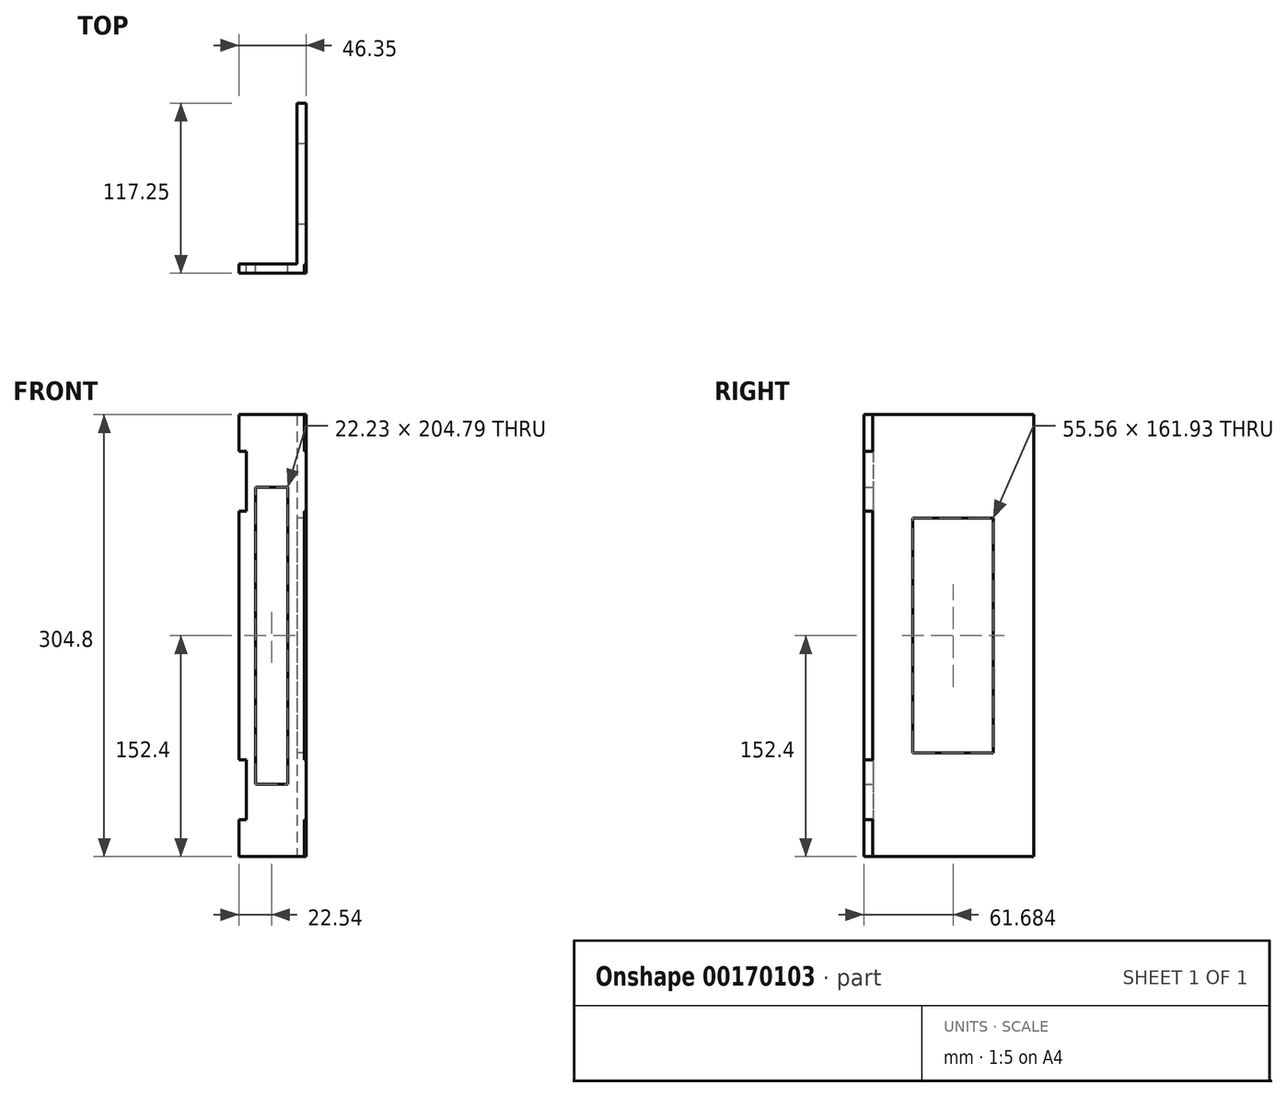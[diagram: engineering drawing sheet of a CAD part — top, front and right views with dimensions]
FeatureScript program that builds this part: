
annotation { "Feature Type Name" : "Feature", "Feature Type Description" : "" }
export const myFeature = defineFeature(function(context is Context, id is Id, definition is map)
    precondition{}
    {
        {
            var Q0;
            Q0=qCreatedBy(makeId("Front.planeOp"),FACE);
            var sketch = newSketch(context, id + "F0", { "sketchPlane" : qUnion([Q0])});
            skLineSegment(sketch, "E0.bottom", {"start": v(-7.94, 85.73) * mm, "end": v(7.94, 85.73) * mm});
            skLineSegment(sketch, "E0.top", {"start": v(-7.94, -85.73) * mm, "end": v(7.94, -85.73) * mm});
            skLineSegment(sketch, "E0.left", {"start": v(-7.94, 85.73) * mm, "end": v(-7.94, -85.73) * mm});
            skLineSegment(sketch, "E0.right", {"start": v(7.94, 85.73) * mm, "end": v(7.94, -85.73) * mm});
            skPoint(sketch, "E0.middle", {"position": v(0, 0) * mm});
            skLineSegment(sketch, "E1.bottom", {"start": v(-11.11, 102.4) * mm, "end": v(11.11, 102.4) * mm});
            skLineSegment(sketch, "E1.top", {"start": v(-11.11, -102.4) * mm, "end": v(11.11, -102.4) * mm});
            skLineSegment(sketch, "E1.left", {"start": v(-11.11, 102.4) * mm, "end": v(-11.11, -102.4) * mm});
            skLineSegment(sketch, "E1.right", {"start": v(11.11, 102.4) * mm, "end": v(11.11, -102.4) * mm});
            skCircle(sketch, "E2", {"center": v(0, 90.49) * mm, "radius": 1.2 * mm});
            skCircle(sketch, "E3.MirrorC", {"center": v(0, -90.49) * mm, "radius": 1.2 * mm});
            skLineSegment(sketch, "E4.bottom", {"start": v(-17.46, 152.4) * mm, "end": v(17.46, 152.4) * mm});
            skLineSegment(sketch, "E4.top", {"start": v(-17.46, -152.4) * mm, "end": v(17.46, -152.4) * mm});
            skLineSegment(sketch, "E4.left", {"start": v(-17.46, 127) * mm, "end": v(-17.46, 85.73) * mm});
            skLineSegment(sketch, "E4.right", {"start": v(17.46, 127) * mm, "end": v(17.46, 85.73) * mm});
            skLineSegment(sketch, "E5.bottom", {"start": v(-17.46, 152.4) * mm, "end": v(-22.54, 152.4) * mm});
            skLineSegment(sketch, "E5.right", {"start": v(-22.54, 152.4) * mm, "end": v(-22.54, 127) * mm});
            skLineSegment(sketch, "E6.bottom", {"start": v(-22.54, 127) * mm, "end": v(-17.46, 127) * mm});
            skLineSegment(sketch, "E6.top", {"start": v(-22.54, 85.73) * mm, "end": v(-17.46, 85.73) * mm});
            skLineSegment(sketch, "E7.trimOffspring", {"start": v(-22.54, 85.73) * mm, "end": v(-22.54, 0) * mm});
            skLineSegment(sketch, "E8.MirrorCS", {"start": v(-22.54, -85.73) * mm, "end": v(-22.54, 0) * mm});
            skLineSegment(sketch, "E9.MirrorCS", {"start": v(-22.54, -85.73) * mm, "end": v(-17.46, -85.73) * mm});
            skLineSegment(sketch, "E10.MirrorCS", {"start": v(-17.46, -152.4) * mm, "end": v(-22.54, -152.4) * mm});
            skLineSegment(sketch, "E11.MirrorCS", {"start": v(-22.54, -152.4) * mm, "end": v(-22.54, -127) * mm});
            skLineSegment(sketch, "E12.MirrorCS", {"start": v(-22.54, -127) * mm, "end": v(-17.46, -127) * mm});
            skLineSegment(sketch, "E13.MirrorCS", {"start": v(17.46, -152.4) * mm, "end": v(22.54, -152.4) * mm});
            skLineSegment(sketch, "E14.MirrorCS", {"start": v(22.54, -152.4) * mm, "end": v(22.54, -127) * mm});
            skLineSegment(sketch, "E15.MirrorCS", {"start": v(22.54, -127) * mm, "end": v(17.46, -127) * mm});
            skLineSegment(sketch, "E16.MirrorCS", {"start": v(22.54, -85.73) * mm, "end": v(17.46, -85.73) * mm});
            skLineSegment(sketch, "E17.MirrorCS", {"start": v(22.54, -85.73) * mm, "end": v(22.54, 0) * mm});
            skLineSegment(sketch, "E18.MirrorCS", {"start": v(22.54, 85.73) * mm, "end": v(22.54, 0) * mm});
            skLineSegment(sketch, "E19.MirrorCS", {"start": v(22.54, 85.73) * mm, "end": v(17.46, 85.73) * mm});
            skLineSegment(sketch, "E20.MirrorCS", {"start": v(22.54, 127) * mm, "end": v(17.46, 127) * mm});
            skLineSegment(sketch, "E21.MirrorCS", {"start": v(17.46, 152.4) * mm, "end": v(22.54, 152.4) * mm});
            skLineSegment(sketch, "E22.MirrorCS", {"start": v(22.54, 152.4) * mm, "end": v(22.54, 127) * mm});
            skLineSegment(sketch, "E23.trimOffspring", {"start": v(-17.46, -85.73) * mm, "end": v(-17.46, -127) * mm});
            skLineSegment(sketch, "E24.trimOffspring", {"start": v(17.46, -85.72) * mm, "end": v(17.46, -127) * mm});
            skSolve(sketch);
        }
        {
            var Q0;
            Q0=makeQuery(id+"F0.imprint","IMPRINT",FACE,{"disambiguationData":[TD([[makeQuery(id+"F0.imprint","IMPRINT",EDGE,{"derivedFrom":sQuery(id+"F0.wireOp",EDGE,"E1.bottom")}),1.0]])]});
            extrude(context, id + "F1", {"entities" : qUnion([Q0]), "depth" : 6.35 * mm});
        }
        {
            var Q0;
            Q0=qCreatedBy(makeId("Right.planeOp"),FACE);
            cPlane(context, id + "F2", {"entities" : qUnion([Q0]), "cplaneType" : CPlaneType.OFFSET, "offset" : 17.46 * mm, "width" : 152.4 * mm, "height" : 152.4 * mm});
        }
        {
            var Q0;
            Q0=qCreatedBy(id+"F2.planeOp",FACE);
            var sketch = newSketch(context, id + "F3", { "sketchPlane" : qUnion([Q0])});
            skLineSegment(sketch, "E25", {"start": v(55.33, 146.13) * mm, "end": v(55.33, -156.26) * mm, "construction": true});
            skLineSegment(sketch, "E26.bottom", {"start": v(27.55, 80.96) * mm, "end": v(83.12, 80.96) * mm});
            skLineSegment(sketch, "E26.top", {"start": v(27.55, -80.96) * mm, "end": v(83.12, -80.96) * mm});
            skLineSegment(sketch, "E26.left", {"start": v(27.55, 80.96) * mm, "end": v(27.55, -80.96) * mm});
            skLineSegment(sketch, "E26.right", {"start": v(83.12, 80.96) * mm, "end": v(83.12, -80.96) * mm});
            skPoint(sketch, "E26.middle", {"position": v(55.33, 0) * mm});
            skCircle(sketch, "E27", {"center": v(55.33, 20.64) * mm, "radius": 19.05 * mm});
            skLineSegment(sketch, "E28.bottom", {"start": v(110.9, 152.4) * mm, "end": v(-0.23, 152.4) * mm});
            skLineSegment(sketch, "E28.top", {"start": v(110.9, -152.4) * mm, "end": v(-0.23, -152.4) * mm});
            skLineSegment(sketch, "E28.left", {"start": v(110.9, 152.4) * mm, "end": v(110.9, -152.4) * mm});
            skLineSegment(sketch, "E28.right", {"start": v(-0.23, 152.4) * mm, "end": v(-0.23, 127) * mm});
            skLineSegment(sketch, "E29.0", {"start": v(-6.35, 127) * mm, "end": v(0, 127) * mm});
            skLineSegment(sketch, "E30.0", {"start": v(-6.35, 85.73) * mm, "end": v(0, 85.73) * mm});
            skLineSegment(sketch, "E31.0", {"start": v(-6.35, -85.73) * mm, "end": v(0, -85.73) * mm});
            skLineSegment(sketch, "E32.0", {"start": v(-6.35, -127) * mm, "end": v(0, -127) * mm});
            skPoint(sketch, "E33.0", {"position": v(-3.18, -152.4) * mm});
            skLineSegment(sketch, "E34.0", {"start": v(-6.35, 127) * mm, "end": v(-6.35, 85.73) * mm});
            skLineSegment(sketch, "E35.trimOffspring", {"start": v(-0.23, 85.72) * mm, "end": v(-0.23, -85.73) * mm});
            skLineSegment(sketch, "E36.0", {"start": v(-6.35, -85.72) * mm, "end": v(-6.35, -127) * mm});
            skLineSegment(sketch, "E37.trimOffspring", {"start": v(-0.23, -127) * mm, "end": v(-0.23, -152.4) * mm});
            skSolve(sketch);
        }
        {
            var Q0;
            Q0 = qSketchRegion(id + "F3", true);
            extrude(context, id + "F4", {"entities" : qUnion([Q0]), "operationType" : NewBodyOperationType.ADD, "depth" : 6.35 * mm});
        }
    });
